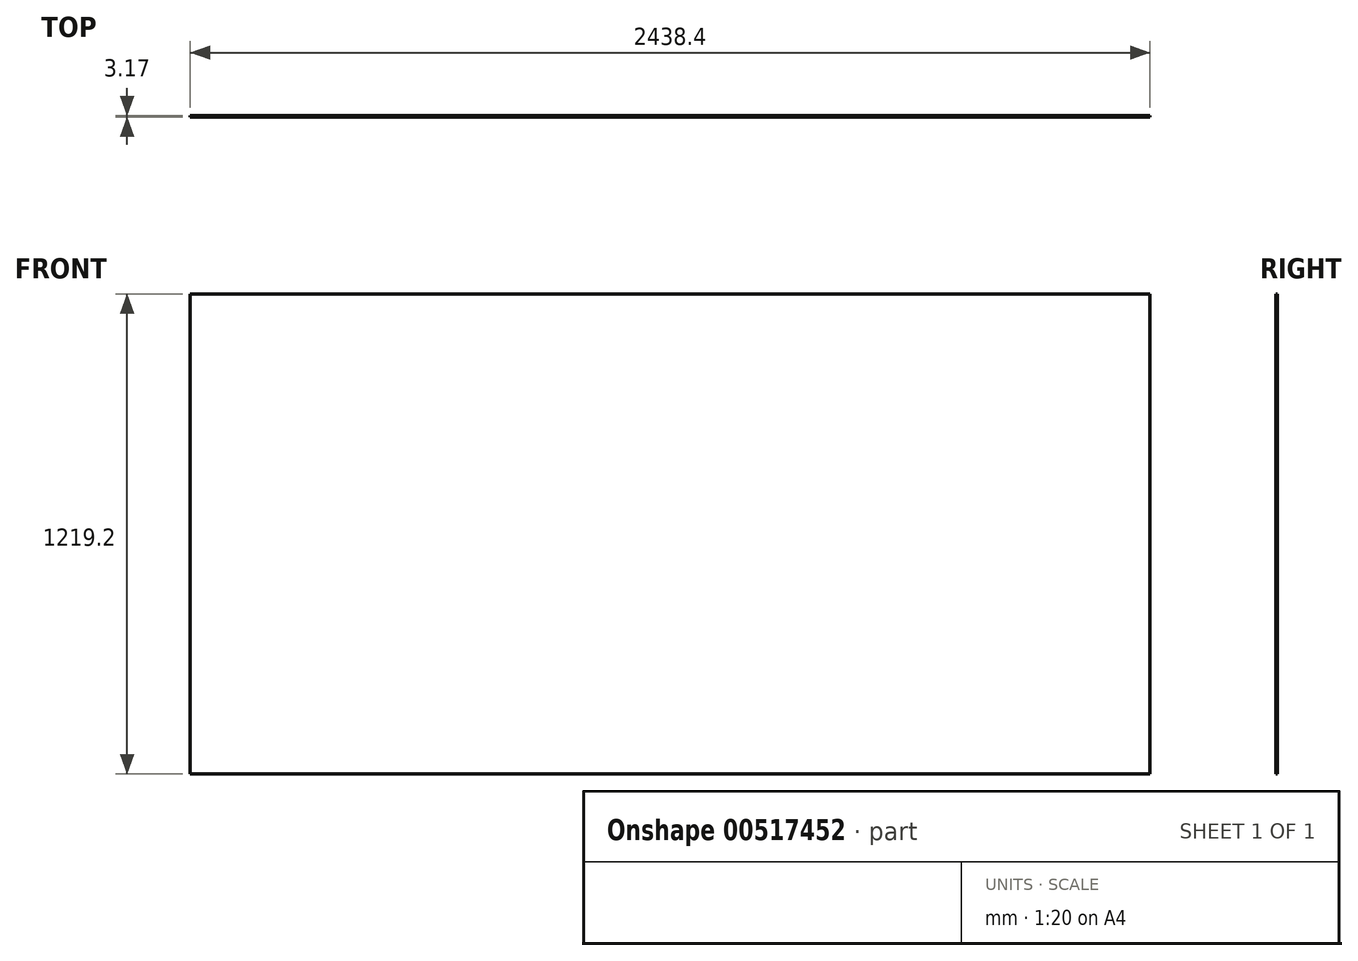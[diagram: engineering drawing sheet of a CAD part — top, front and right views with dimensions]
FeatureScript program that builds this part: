
annotation { "Feature Type Name" : "Feature", "Feature Type Description" : "" }
export const myFeature = defineFeature(function(context is Context, id is Id, definition is map)
    precondition{}
    {
        {
            var Q0;
            Q0=qCreatedBy(makeId("Front.planeOp"),FACE);
            var sketch = newSketch(context, id + "F0", { "sketchPlane" : qUnion([Q0])});
            skLineSegment(sketch, "E0.bottom", {"start": v(1219.2, -609.6) * mm, "end": v(-1219.2, -609.6) * mm});
            skLineSegment(sketch, "E0.top", {"start": v(1219.2, 609.6) * mm, "end": v(-1219.2, 609.6) * mm});
            skLineSegment(sketch, "E0.left", {"start": v(1219.2, -609.6) * mm, "end": v(1219.2, 609.6) * mm});
            skLineSegment(sketch, "E0.right", {"start": v(-1219.2, -609.6) * mm, "end": v(-1219.2, 609.6) * mm});
            skPoint(sketch, "E0.middle", {"position": v(0, 0) * mm});
            skSolve(sketch);
        }
        {
            var Q0;
            Q0 = qSketchRegion(id + "F0", true);
            extrude(context, id + "F1", {"entities" : qUnion([Q0]), "depth" : 3.17 * mm, "offsetDistance" : 25.4 * mm});
        }
    });
